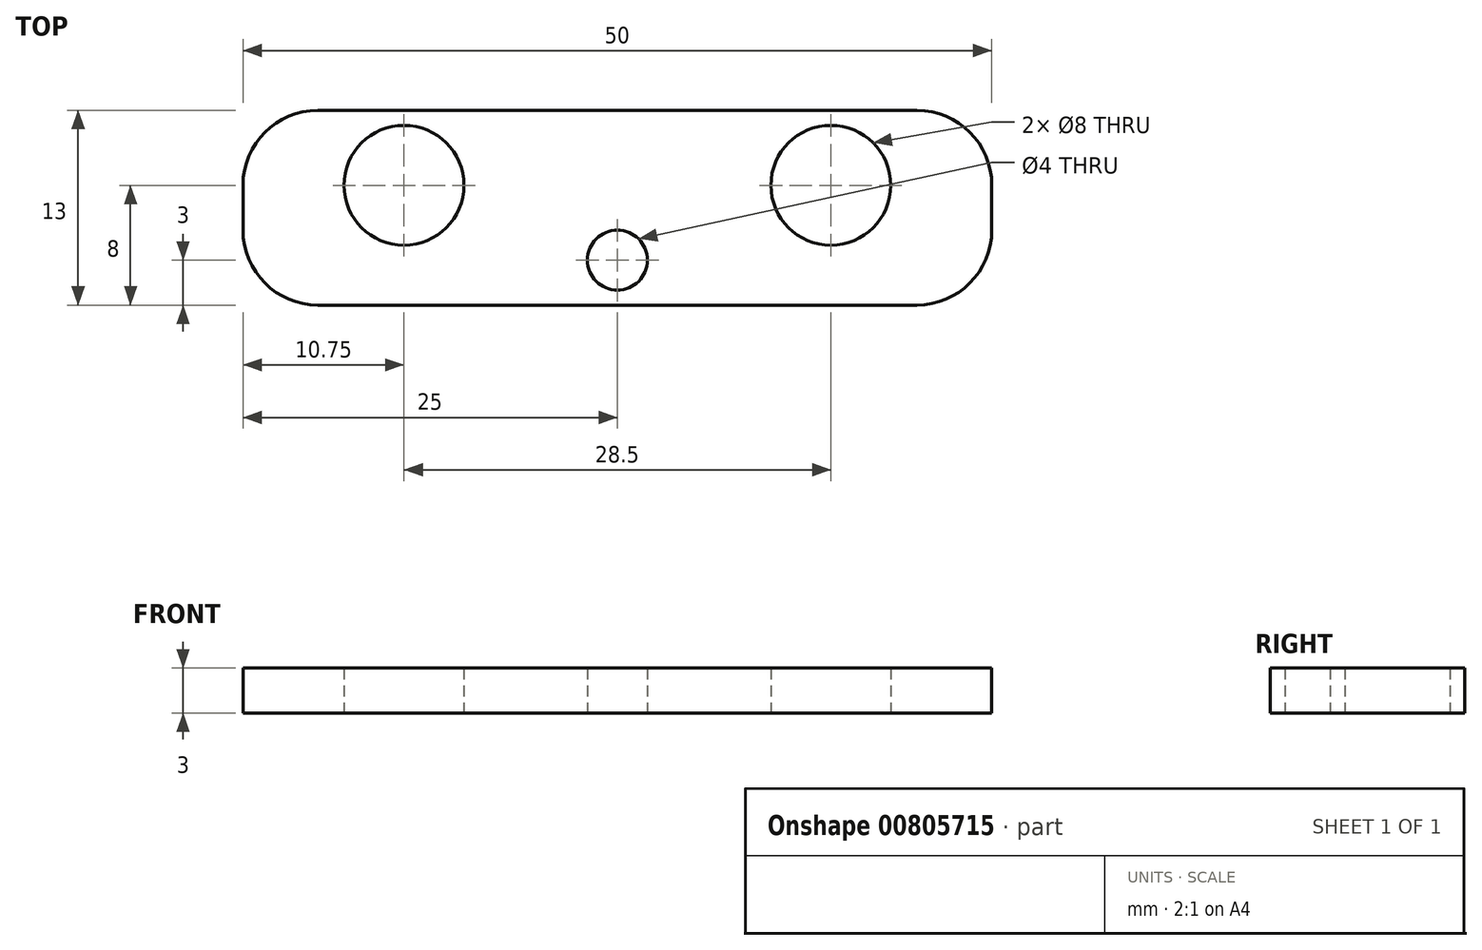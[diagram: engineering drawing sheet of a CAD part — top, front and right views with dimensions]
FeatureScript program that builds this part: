
annotation { "Feature Type Name" : "Feature", "Feature Type Description" : "" }
export const myFeature = defineFeature(function(context is Context, id is Id, definition is map)
    precondition{}
    {
        {
            var Q0;
            Q0=qCreatedBy(makeId("Top.planeOp"),FACE);
            var sketch = newSketch(context, id + "F0", { "sketchPlane" : qUnion([Q0])});
            skPoint(sketch, "E0.middle", {"position": v(0, 0) * mm});
            skCircle(sketch, "E1", {"center": v(0, -3) * mm, "radius": 2 * mm});
            skLineSegment(sketch, "E2.bottom", {"start": v(-25, 7) * mm, "end": v(25, 7) * mm});
            skLineSegment(sketch, "E2.top", {"start": v(-25, -6) * mm, "end": v(25, -6) * mm});
            skLineSegment(sketch, "E2.left", {"start": v(-25, 7) * mm, "end": v(-25, -6) * mm});
            skLineSegment(sketch, "E2.right", {"start": v(25, 7) * mm, "end": v(25, -6) * mm});
            skCircle(sketch, "E3", {"center": v(-14.25, 2) * mm, "radius": 4 * mm});
            skCircle(sketch, "E4", {"center": v(14.25, 2) * mm, "radius": 4 * mm});
            skSolve(sketch);
        }
        {
            var Q0;
            Q0=makeQuery(id+"F0.imprint","IMPRINT",FACE,{"disambiguationData":[TD([[makeQuery(id+"F0.imprint","IMPRINT",EDGE,{"derivedFrom":sQuery(id+"F0.wireOp",EDGE,"E1")}),-1.0]])]});
            extrude(context, id + "F1", {"entities" : qUnion([Q0]), "depth" : 3 * mm, "offsetDistance" : 25 * mm});
        }
        {
            var Q0;
            Q0=makeQuery(id+"F1.opExtrude","SWEPT_EDGE",EDGE,{"disambiguationData":[OSD([sQuery(id+"F0.wireOp",EDGE,"E2.bottom"),sQuery(id+"F0.wireOp",EDGE,"E2.left")])]});
            var Q1;
            Q1=makeQuery(id+"F1.opExtrude","SWEPT_EDGE",EDGE,{"disambiguationData":[OSD([sQuery(id+"F0.wireOp",EDGE,"E2.top"),sQuery(id+"F0.wireOp",EDGE,"E2.left")])]});
            var Q2;
            Q2=makeQuery(id+"F1.opExtrude","SWEPT_EDGE",EDGE,{"disambiguationData":[OSD([sQuery(id+"F0.wireOp",EDGE,"E2.top"),sQuery(id+"F0.wireOp",EDGE,"E2.right")])]});
            var Q3;
            Q3=makeQuery(id+"F1.opExtrude","SWEPT_EDGE",EDGE,{"disambiguationData":[OSD([sQuery(id+"F0.wireOp",EDGE,"E2.bottom"),sQuery(id+"F0.wireOp",EDGE,"E2.right")])]});
            fillet(context, id + "F2", {"entities" : qUnion([Q0, Q1, Q2, Q3]), "radius" : 5 * mm, "tangentPropagation" : true, "allowEdgeOverflow" : false});
        }
    });
